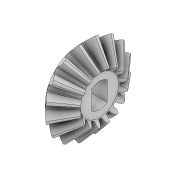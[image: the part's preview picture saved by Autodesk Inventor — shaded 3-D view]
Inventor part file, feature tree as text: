
AUTODESK INVENTOR PART (.ipt)
format: ipt  version: 2020 (Build 240168000, 168)  size: 870,912 bytes
history: native  units: in
note: dims shown in document units (in); Inventor stores cm internally (conversion verified against a paired STEP export)
features: other x3, extrude x1, sketch x1
ambient origin geometry x8: Origin, YZ Plane, XZ Plane, XY Plane, X Axis, Y Axis, Z Axis, Center Point
bodies: Solid1 (feature_tree)
feature tree (5):
  other  "straight_miter_gear_isoiso_-_st.ipt"
  extrude  "Extrusion1"  Depth=0.122in
  other  "Solid1::straight_miter_gear_isoiso_-_st.ipt"
  other  "TaggingFeature1"
  sketch  "Sketch1"  dims[d0=0.0394in d1=0.122in d2=0.061in d3=1.0in d4=0.0in]
